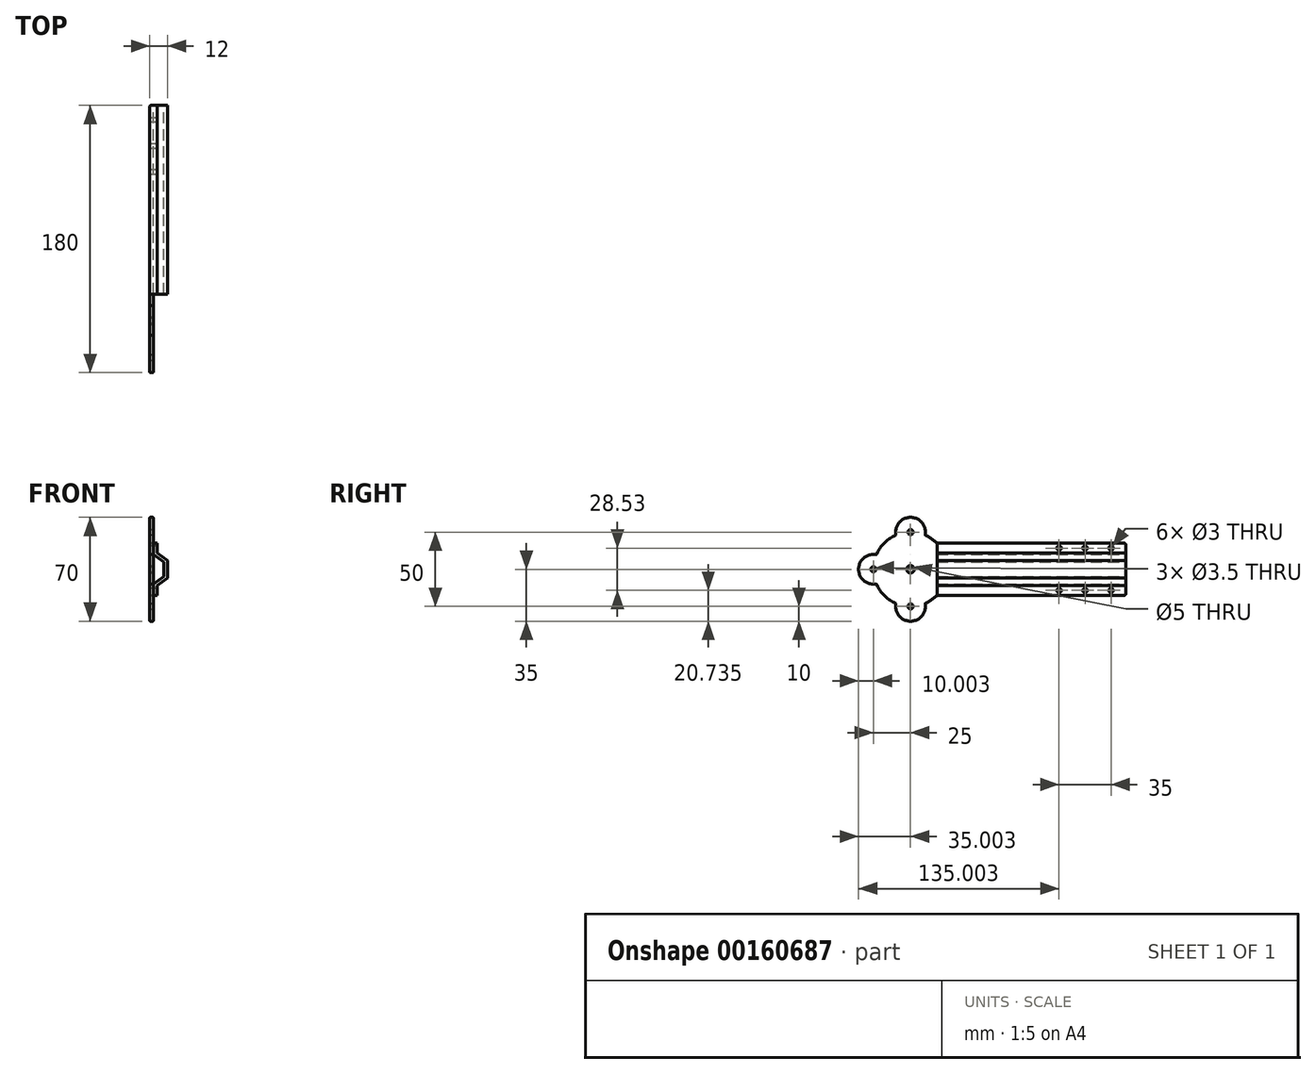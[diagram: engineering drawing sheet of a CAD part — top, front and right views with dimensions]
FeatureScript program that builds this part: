
annotation { "Feature Type Name" : "Feature", "Feature Type Description" : "" }
export const myFeature = defineFeature(function(context is Context, id is Id, definition is map)
    precondition{}
    {
        {
            var Q0;
            Q0=qCreatedBy(makeId("Right.planeOp"),FACE);
            var sketch = newSketch(context, id + "F0", { "sketchPlane" : qUnion([Q0])});
            skArc(sketch, "E0", {"start": v(-63.57, 17.5) * mm, "mid": v(-106.43, 0) * mm, "end": v(-63.57, -17.5) * mm});
            skLineSegment(sketch, "E1.bottom", {"start": v(63.57, -17.5) * mm, "end": v(-63.57, -17.5) * mm});
            skLineSegment(sketch, "E1.top", {"start": v(63.57, 17.5) * mm, "end": v(-63.57, 17.5) * mm});
            skLineSegment(sketch, "E1.left", {"start": v(63.57, -17.5) * mm, "end": v(63.57, 17.5) * mm});
            skPoint(sketch, "E1.middle", {"position": v(0, 0) * mm});
            skSolve(sketch);
        }
        {
            var Q0;
            Q0=makeQuery(id+"F0.imprint","IMPRINT",FACE,{"disambiguationData":[TD([[makeQuery(id+"F0.imprint","IMPRINT",EDGE,{"derivedFrom":sQuery(id+"F0.wireOp",EDGE,"E0")}),1.0]])]});
            var sketch = newSketch(context, id + "F1", { "sketchPlane" : qUnion([Q0])});
            skLineSegment(sketch, "E2.0.0", {"start": v(63.57, 17.5) * mm, "end": v(-63.57, 17.5) * mm});
            skLineSegment(sketch, "E2.0.2", {"start": v(-63.57, -17.5) * mm, "end": v(63.57, -17.5) * mm});
            skLineSegment(sketch, "E2.0.3", {"start": v(63.57, -17.5) * mm, "end": v(63.57, 17.5) * mm});
            skLineSegment(sketch, "E3", {"start": v(-63.57, 17.5) * mm, "end": v(-63.57, -17.5) * mm});
            skSolve(sketch);
        }
        {
            var Q0;
            Q0=qSketchRegion(id+"F1",true);
            extrude(context, id + "F2", {"entities" : qUnion([Q0]), "depth" : 9.5 * mm});
        }
        {
            var Q0;
            Q0=qSketchRegion(id+"F0",true);
            extrude(context, id + "F3", {"entities" : qUnion([Q0]), "operationType" : NewBodyOperationType.ADD, "oppositeDirection" : true, "depth" : 2.5 * mm});
        }
        {
            var Q0;
            Q0=makeQuery(id+"F2.opExtrude","SWEPT_FACE",FACE,{"disambiguationData":[OSD([sQuery(id+"F1.wireOp",EDGE,"E2.0.3")])]});
            var sketch = newSketch(context, id + "F4", { "sketchPlane" : qUnion([Q0])});
            skLineSegment(sketch, "E4", {"start": v(0, -10) * mm, "end": v(-7, -5) * mm});
            skLineSegment(sketch, "E5", {"start": v(-7, -5) * mm, "end": v(-7, 5) * mm});
            skLineSegment(sketch, "E6", {"start": v(-7, 5) * mm, "end": v(0, 10) * mm});
            skLineSegment(sketch, "E7", {"start": v(0, -10) * mm, "end": v(0, 10) * mm});
            skSolve(sketch);
        }
        {
            var Q0;
            Q0=qSketchRegion(id+"F0",true);
            extrude(context, id + "F5", {"entities" : qUnion([Q0]), "operationType" : NewBodyOperationType.ADD, "oppositeDirection" : true, "depth" : 2.5 * mm});
        }
        {
            var Q0;
            Q0=qSketchRegion(id+"F4",true);
            extrude(context, id + "F6", {"entities" : qUnion([Q0]), "operationType" : NewBodyOperationType.REMOVE, "oppositeDirection" : true, "depth" : 127.15 * mm});
        }
        {
            var Q0;
            Q0=makeQuery(id+"F3.boolean.opBoolean","MERGE",FACE,{"derivedFrom":[makeQuery(id+"F2.opExtrude","SWEPT_FACE",FACE,{"disambiguationData":[OSD([sQuery(id+"F1.wireOp",EDGE,"E2.0.3")])]}),makeQuery(id+"F3.opExtrude","SWEPT_FACE",FACE,{"disambiguationData":[OSD([sQuery(id+"F0.wireOp",EDGE,"E1.left")])]})]});
            var sketch = newSketch(context, id + "F7", { "sketchPlane" : qUnion([Q0])});
            skLineSegment(sketch, "E8", {"start": v(-2.5, -17.5) * mm, "end": v(-2.5, -11.03) * mm});
            skLineSegment(sketch, "E9", {"start": v(-2.5, -11.03) * mm, "end": v(-9.5, -6) * mm});
            skLineSegment(sketch, "E10", {"start": v(-9.5, -6) * mm, "end": v(-9.5, -17.5) * mm});
            skLineSegment(sketch, "E11", {"start": v(-9.5, -17.5) * mm, "end": v(-2.5, -17.5) * mm});
            skLineSegment(sketch, "E12.MirrorCS", {"start": v(-9.5, 17.5) * mm, "end": v(-2.5, 17.5) * mm});
            skLineSegment(sketch, "E13.MirrorCS", {"start": v(-2.5, 17.5) * mm, "end": v(-2.5, 11.03) * mm});
            skLineSegment(sketch, "E14.MirrorCS", {"start": v(-2.5, 11.03) * mm, "end": v(-9.5, 6) * mm});
            skLineSegment(sketch, "E15.MirrorCS", {"start": v(-9.5, 6) * mm, "end": v(-9.5, 17.5) * mm});
            skSolve(sketch);
        }
        {
            var Q0;
            Q0=qSketchRegion(id+"F7",true);
            extrude(context, id + "F8", {"entities" : qUnion([Q0]), "operationType" : NewBodyOperationType.REMOVE, "oppositeDirection" : true, "depth" : 127.15 * mm});
        }
        {
            var Q0;
            Q0=makeQuery(id+"F3.opExtrude","CAP_FACE",FACE,{"disambiguationData":[OSD([sQuery(id+"F0.wireOp",EDGE,"E0"),sQuery(id+"F0.wireOp",EDGE,"E1.bottom"),sQuery(id+"F0.wireOp",EDGE,"E1.top"),sQuery(id+"F0.wireOp",EDGE,"E1.left")])],"isStart":false});
            var sketch = newSketch(context, id + "F9", { "sketchPlane" : qUnion([Q0])});
            skLineSegment(sketch, "E16", {"start": v(81.43, 15) * mm, "end": v(81.43, 25) * mm});
            skLineSegment(sketch, "E17", {"start": v(81.43, -15) * mm, "end": v(81.43, -25) * mm});
            skCircle(sketch, "E18", {"center": v(81.43, -25) * mm, "radius": 10 * mm});
            skCircle(sketch, "E19", {"center": v(81.43, 25) * mm, "radius": 10 * mm});
            skCircle(sketch, "E20", {"center": v(106.43, 0) * mm, "radius": 10 * mm});
            skPoint(sketch, "E21.orphan", {"position": v(81.43, 0) * mm});
            skSolve(sketch);
        }
        {
            var Q0;
            Q0=makeQuery(id+"FsFJ8rt28dWSZyA_1.boolean.opBoolean","MERGE",FACE,{"derivedFrom":[makeQuery(id+"F3.opExtrude","CAP_FACE",FACE,{"disambiguationData":[OSD([sQuery(id+"F0.wireOp",EDGE,"E0"),sQuery(id+"F0.wireOp",EDGE,"E1.bottom"),sQuery(id+"F0.wireOp",EDGE,"E1.top"),sQuery(id+"F0.wireOp",EDGE,"E1.left")])],"isStart":false}),makeQuery(id+"FsFJ8rt28dWSZyA_1.opExtrude","CAP_FACE",FACE,{"disambiguationData":[OSD([sQuery(id+"F9.wireOp",EDGE,"E18")])],"isStart":true}),makeQuery(id+"FsFJ8rt28dWSZyA_1.opExtrude","CAP_FACE",FACE,{"disambiguationData":[OSD([sQuery(id+"F9.wireOp",EDGE,"E19")])],"isStart":true}),makeQuery(id+"FsFJ8rt28dWSZyA_1.opExtrude","CAP_FACE",FACE,{"disambiguationData":[OSD([sQuery(id+"F9.wireOp",EDGE,"E20")])],"isStart":true})]});
            var sketch = newSketch(context, id + "F10", { "sketchPlane" : qUnion([Q0])});
            skLineSegment(sketch, "E22", {"start": v(-8.57, -23.41) * mm, "end": v(-8.57, 34.28) * mm, "construction": true});
            skLineSegment(sketch, "E23", {"start": v(-8.3, 0) * mm, "end": v(-87.07, 0) * mm, "construction": true});
            skCircle(sketch, "E24", {"center": v(-18.57, -14.26) * mm, "radius": 1.5 * mm});
            skCircle(sketch, "E25", {"center": v(-36.07, -14.27) * mm, "radius": 1.5 * mm});
            skCircle(sketch, "E26", {"center": v(-53.57, -14.27) * mm, "radius": 1.5 * mm});
            skCircle(sketch, "E27.MirrorC", {"center": v(-18.57, 14.27) * mm, "radius": 1.5 * mm});
            skCircle(sketch, "E28.MirrorC", {"center": v(-36.07, 14.27) * mm, "radius": 1.5 * mm});
            skCircle(sketch, "E29.MirrorC", {"center": v(-53.57, 14.27) * mm, "radius": 1.5 * mm});
            skSolve(sketch);
        }
        {
            var Q0;
            Q0=qSketchRegion(id+"F10",true);
            extrude(context, id + "F11", {"entities" : qUnion([Q0]), "operationType" : NewBodyOperationType.REMOVE, "oppositeDirection" : true, "depth" : 5 * mm});
        }
        {
            var Q0;
            Q0=qSketchRegion(id+"F9",true);
            extrude(context, id + "F12", {"entities" : qUnion([Q0]), "operationType" : NewBodyOperationType.ADD, "oppositeDirection" : true, "depth" : 2.5 * mm});
        }
        {
            var Q0;
            Q0=makeQuery(id+"F12.boolean.opBoolean","MERGE",FACE,{"derivedFrom":[makeQuery(id+"F6.boolean.opBoolean","MERGE",FACE,{"derivedFrom":[makeQuery(id+"F3.opExtrude","CAP_FACE",FACE,{"disambiguationData":[OSD([sQuery(id+"F0.wireOp",EDGE,"E0"),sQuery(id+"F0.wireOp",EDGE,"E1.bottom"),sQuery(id+"F0.wireOp",EDGE,"E1.top"),sQuery(id+"F0.wireOp",EDGE,"E1.left")])],"isStart":true}),makeQuery(id+"F6.opExtrude","SWEPT_FACE",FACE,{"disambiguationData":[OSD([sQuery(id+"F4.wireOp",EDGE,"E7")])]})]}),makeQuery(id+"F12.opExtrude","CAP_FACE",FACE,{"disambiguationData":[OSD([sQuery(id+"F9.wireOp",EDGE,"E18")])],"isStart":false}),makeQuery(id+"F12.opExtrude","CAP_FACE",FACE,{"disambiguationData":[OSD([sQuery(id+"F9.wireOp",EDGE,"E19")])],"isStart":false}),makeQuery(id+"F12.opExtrude","CAP_FACE",FACE,{"disambiguationData":[OSD([sQuery(id+"F9.wireOp",EDGE,"E20")])],"isStart":false})]});
            var sketch = newSketch(context, id + "F13", { "sketchPlane" : qUnion([Q0])});
            skCircle(sketch, "E30", {"center": v(-81.43, 0) * mm, "radius": 2.5 * mm});
            skCircle(sketch, "E31", {"center": v(-81.43, 25) * mm, "radius": 1.75 * mm});
            skCircle(sketch, "E32", {"center": v(-106.43, 0) * mm, "radius": 1.75 * mm});
            skCircle(sketch, "E33", {"center": v(-81.43, -25) * mm, "radius": 1.75 * mm});
            skSolve(sketch);
        }
        {
            var Q0;
            Q0=qSketchRegion(id+"F13",true);
            extrude(context, id + "F14", {"entities" : qUnion([Q0]), "operationType" : NewBodyOperationType.REMOVE, "oppositeDirection" : true, "depth" : 2.5 * mm});
        }
        {
            var Q0;
            Q0=makeQuery(id+"F8.boolean.opBoolean","COPY",EDGE,{"derivedFrom":makeQuery(id+"F8.opExtrude","SWEPT_EDGE",EDGE,{"disambiguationData":[OSD([sQuery(id+"F0.wireOp",EDGE,"E1.top"),sQuery(id+"F0.wireOp",EDGE,"E1.left"),sQuery(id+"F1.wireOp",EDGE,"E2.0.0"),sQuery(id+"F1.wireOp",EDGE,"E2.0.3"),sQuery(id+"F7.wireOp",EDGE,"E12.MirrorCS"),sQuery(id+"F7.wireOp",EDGE,"E13.MirrorCS")])]})});
            var Q1;
            Q1=makeQuery(id+"F3.opExtrude","CAP_EDGE",EDGE,{"disambiguationData":[OSD([sQuery(id+"F0.wireOp",EDGE,"E1.top")])],"isStart":false});
            var Q2;
            Q2=makeQuery(id+"F3.opExtrude","CAP_EDGE",EDGE,{"disambiguationData":[OSD([sQuery(id+"F0.wireOp",EDGE,"E1.left")])],"isStart":false});
            var Q3;
            Q3=makeQuery(id+"F3.opExtrude","CAP_EDGE",EDGE,{"disambiguationData":[OSD([sQuery(id+"F0.wireOp",EDGE,"E1.bottom")])],"isStart":false});
            var Q4;
            Q4=makeQuery(id+"F8.boolean.opBoolean","COPY",EDGE,{"derivedFrom":makeQuery(id+"F8.opExtrude","SWEPT_EDGE",EDGE,{"disambiguationData":[OSD([sQuery(id+"F0.wireOp",EDGE,"E1.bottom"),sQuery(id+"F0.wireOp",EDGE,"E1.left"),sQuery(id+"F1.wireOp",EDGE,"E2.0.2"),sQuery(id+"F1.wireOp",EDGE,"E2.0.3"),sQuery(id+"F7.wireOp",EDGE,"E8"),sQuery(id+"F7.wireOp",EDGE,"E11")])]})});
            var Q5;
            Q5=makeQuery(id+"F3.boolean.opBoolean","MERGE",EDGE,{"derivedFrom":[makeQuery(id+"F2.opExtrude","SWEPT_EDGE",EDGE,{"disambiguationData":[OSD([sQuery(id+"F1.wireOp",EDGE,"E2.0.2"),sQuery(id+"F1.wireOp",EDGE,"E2.0.3")])]}),makeQuery(id+"F3.opExtrude","SWEPT_EDGE",EDGE,{"disambiguationData":[OSD([sQuery(id+"F0.wireOp",EDGE,"E1.bottom"),sQuery(id+"F0.wireOp",EDGE,"E1.left")])]})]});
            var Q6;
            Q6=makeQuery(id+"F3.boolean.opBoolean","MERGE",EDGE,{"derivedFrom":[makeQuery(id+"F2.opExtrude","SWEPT_EDGE",EDGE,{"disambiguationData":[OSD([sQuery(id+"F1.wireOp",EDGE,"E2.0.0"),sQuery(id+"F1.wireOp",EDGE,"E2.0.3")])]}),makeQuery(id+"F3.opExtrude","SWEPT_EDGE",EDGE,{"disambiguationData":[OSD([sQuery(id+"F0.wireOp",EDGE,"E1.top"),sQuery(id+"F0.wireOp",EDGE,"E1.left")])]})]});
            fillet(context, id + "F15", {"entities" : qUnion([Q0, Q1, Q2, Q3, Q4, Q5, Q6]), "radius" : 1 * mm, "tangentPropagation" : true, "allowEdgeOverflow" : false});
        }
        {
            var Q0;
            Q0=makeQuery(id+"F12.opExtrude","SWEPT_FACE",FACE,{"disambiguationData":[OSD([sQuery(id+"F9.wireOp",EDGE,"E18")])]});
            var Q1;
            Q1=makeQuery(id+"F12.opExtrude","SWEPT_FACE",FACE,{"disambiguationData":[OSD([sQuery(id+"F9.wireOp",EDGE,"E20")])]});
            var Q2;
            Q2=makeQuery(id+"F12.opExtrude","SWEPT_FACE",FACE,{"disambiguationData":[OSD([sQuery(id+"F9.wireOp",EDGE,"E19")])]});
            fillet(context, id + "F16", {"entities" : qUnion([Q0, Q1, Q2]), "radius" : 0.5 * mm, "tangentPropagation" : true, "allowEdgeOverflow" : false});
        }
    });
